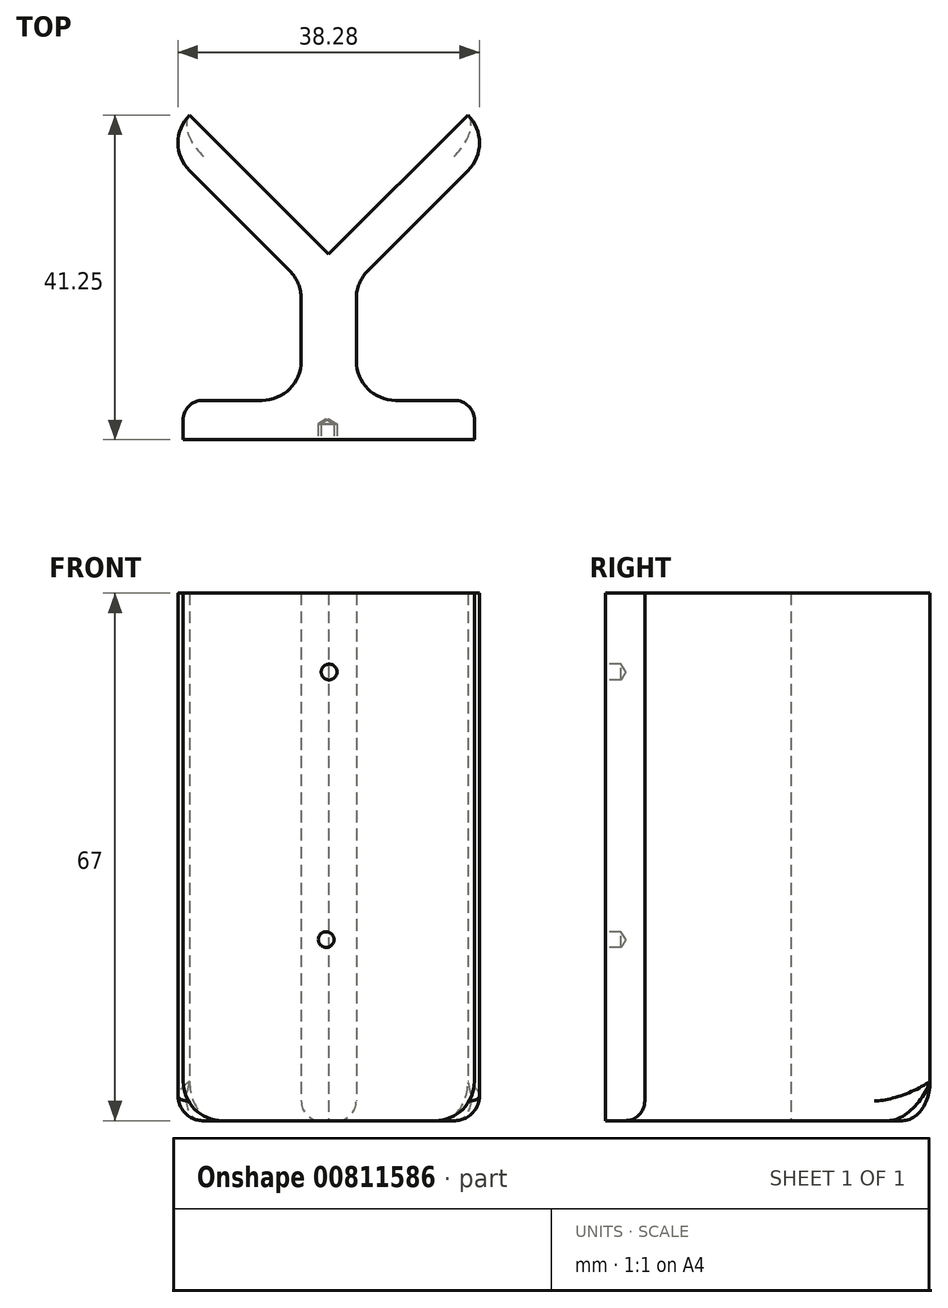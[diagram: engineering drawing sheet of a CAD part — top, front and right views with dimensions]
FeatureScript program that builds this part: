
annotation { "Feature Type Name" : "Feature", "Feature Type Description" : "" }
export const myFeature = defineFeature(function(context is Context, id is Id, definition is map)
    precondition{}
    {
        {
            var Q0;
            Q0=qCreatedBy(makeId("Top.planeOp"),FACE);
            var sketch = newSketch(context, id + "F0", { "sketchPlane" : qUnion([Q0])});
            skLineSegment(sketch, "E0", {"start": v(0, 0) * mm, "end": v(37, 0) * mm});
            skLineSegment(sketch, "E1", {"start": v(37, 0) * mm, "end": v(37, 5) * mm});
            skLineSegment(sketch, "E2", {"start": v(37, 5) * mm, "end": v(22, 5) * mm});
            skLineSegment(sketch, "E3", {"start": v(22, 5) * mm, "end": v(22, 20) * mm});
            skLineSegment(sketch, "E4", {"start": v(22, 20) * mm, "end": v(39.71, 37.71) * mm});
            skLineSegment(sketch, "E5", {"start": v(39.71, 37.71) * mm, "end": v(36.18, 41.25) * mm});
            skLineSegment(sketch, "E6", {"start": v(36.18, 41.25) * mm, "end": v(18.5, 23.57) * mm});
            skLineSegment(sketch, "E7", {"start": v(18.5, 23.57) * mm, "end": v(0.82, 41.25) * mm});
            skLineSegment(sketch, "E8", {"start": v(0.82, 41.25) * mm, "end": v(-2.71, 37.71) * mm});
            skLineSegment(sketch, "E9", {"start": v(-2.71, 37.71) * mm, "end": v(15, 20) * mm});
            skLineSegment(sketch, "E10", {"start": v(15, 20) * mm, "end": v(15, 5) * mm});
            skLineSegment(sketch, "E11", {"start": v(15, 5) * mm, "end": v(0, 5) * mm});
            skLineSegment(sketch, "E12", {"start": v(0, 5) * mm, "end": v(0, 0) * mm});
            skSolve(sketch);
        }
        {
            var Q0;
            Q0=makeQuery(id+"F0.imprint","IMPRINT",FACE,{"disambiguationData":[TD([[makeQuery(id+"F0.imprint","IMPRINT",EDGE,{"derivedFrom":sQuery(id+"F0.wireOp",EDGE,"E0")}),1.0]])]});
            extrude(context, id + "F1", {"entities" : qUnion([Q0]), "depth" : 67 * mm, "offsetDistance" : 25 * mm});
        }
        {
            var Q0;
            Q0=makeQuery(id+"F1.opExtrude","CAP_EDGE",EDGE,{"disambiguationData":[OSD([sQuery(id+"F0.wireOp",EDGE,"E1")])],"isStart":true});
            var Q1;
            Q1=makeQuery(id+"F1.opExtrude","CAP_EDGE",EDGE,{"disambiguationData":[OSD([sQuery(id+"F0.wireOp",EDGE,"E12")])],"isStart":true});
            fillet(context, id + "F2", {"entities" : qUnion([Q0, Q1]), "radius" : 5 * mm, "tangentPropagation" : true, "allowEdgeOverflow" : false});
        }
        {
            var Q0;
            Q0=makeQuery(id+"F1.opExtrude","SWEPT_EDGE",EDGE,{"disambiguationData":[OSD([sQuery(id+"F0.wireOp",EDGE,"E3"),sQuery(id+"F0.wireOp",EDGE,"E4")])]});
            var Q1;
            Q1=makeQuery(id+"F1.opExtrude","SWEPT_EDGE",EDGE,{"disambiguationData":[OSD([sQuery(id+"F0.wireOp",EDGE,"E9"),sQuery(id+"F0.wireOp",EDGE,"E10")])]});
            var Q2;
            Q2=makeQuery(id+"F1.opExtrude","SWEPT_EDGE",EDGE,{"disambiguationData":[OSD([sQuery(id+"F0.wireOp",EDGE,"E2"),sQuery(id+"F0.wireOp",EDGE,"E3")])]});
            var Q3;
            Q3=makeQuery(id+"F1.opExtrude","SWEPT_EDGE",EDGE,{"disambiguationData":[OSD([sQuery(id+"F0.wireOp",EDGE,"E10"),sQuery(id+"F0.wireOp",EDGE,"E11")])]});
            fillet(context, id + "F3", {"entities" : qUnion([Q0, Q1, Q2, Q3]), "radius" : 5 * mm, "tangentPropagation" : true, "allowEdgeOverflow" : false});
        }
        {
            var Q0;
            Q0=makeQuery(id+"F1.opExtrude","SWEPT_EDGE",EDGE,{"disambiguationData":[OSD([sQuery(id+"F0.wireOp",EDGE,"E11"),sQuery(id+"F0.wireOp",EDGE,"E12")])]});
            var Q1;
            Q1=makeQuery(id+"F1.opExtrude","SWEPT_EDGE",EDGE,{"disambiguationData":[OSD([sQuery(id+"F0.wireOp",EDGE,"E1"),sQuery(id+"F0.wireOp",EDGE,"E2")])]});
            fillet(context, id + "F4", {"entities" : qUnion([Q0, Q1]), "radius" : 2.5 * mm, "tangentPropagation" : true, "allowEdgeOverflow" : false});
        }
        {
            var Q0;
            Q0=makeQuery(id+"F1.opExtrude","SWEPT_EDGE",EDGE,{"disambiguationData":[OSD([sQuery(id+"F0.wireOp",EDGE,"E8"),sQuery(id+"F0.wireOp",EDGE,"E9")])]});
            var Q1;
            Q1=makeQuery(id+"F1.opExtrude","SWEPT_EDGE",EDGE,{"disambiguationData":[OSD([sQuery(id+"F0.wireOp",EDGE,"E4"),sQuery(id+"F0.wireOp",EDGE,"E5")])]});
            fillet(context, id + "F5", {"entities" : qUnion([Q0, Q1]), "radius" : 5 * mm, "tangentPropagation" : true, "allowEdgeOverflow" : false});
        }
        {
            var Q0;
            Q0=makeQuery(id+"F1.opExtrude","SWEPT_FACE",FACE,{"disambiguationData":[OSD([sQuery(id+"F0.wireOp",EDGE,"E0")])]});
            var sketch = newSketch(context, id + "F6", { "sketchPlane" : qUnion([Q0])});
            skCircle(sketch, "E13", {"center": v(18.55, 57) * mm, "radius": 1 * mm});
            skCircle(sketch, "E14.1.0.0", {"center": v(18.17, 23) * mm, "radius": 1 * mm});
            skLineSegment(sketch, "E14.direction1", {"start": v(18.55, 57) * mm, "end": v(18.17, 23) * mm, "construction": true});
            skSolve(sketch);
        }
        {
            var Q0;
            Q0=sQuery(id+"F6.wireOp",VERTEX,"E14.direction1.start");
            var Q1;
            Q1=sQuery(id+"F6.wireOp",VERTEX,"E14.direction1.end");
            var Q2;
            Q2=makeQuery(id+"F1.opExtrude","SWEPT_BODY",BODY,{"disambiguationData":[OSD([sQuery(id+"F0.wireOp",EDGE,"E0"),sQuery(id+"F0.wireOp",EDGE,"E1"),sQuery(id+"F0.wireOp",EDGE,"E2"),sQuery(id+"F0.wireOp",EDGE,"E3"),sQuery(id+"F0.wireOp",EDGE,"E4"),sQuery(id+"F0.wireOp",EDGE,"E5"),sQuery(id+"F0.wireOp",EDGE,"E6"),sQuery(id+"F0.wireOp",EDGE,"E7"),sQuery(id+"F0.wireOp",EDGE,"E8"),sQuery(id+"F0.wireOp",EDGE,"E9"),sQuery(id+"F0.wireOp",EDGE,"E10"),sQuery(id+"F0.wireOp",EDGE,"E11"),sQuery(id+"F0.wireOp",EDGE,"E12")])]});
            hole(context, id + "F7", {"style" : HoleStyle.SIMPLE, "endStyle" : HoleEndStyle.BLIND, "holeDiameter" : 2 * mm, "majorDiameter" : 5 * mm, "holeDepth" : 2 * mm, "isTappedThrough" : true, "tappedDepth" : 12 * mm, "tapClearance" : 3, "locations" : qUnion([Q0, Q1]), "scope" : qUnion([Q2])});
        }
    });
